# Revit family: Deca_Tubo de Ligação com Anel Expansor _1968.C.KID_Bacia Infantil
name_source: partatom
category: Plumbing Fixtures
revit_build: Autodesk Revit Architecture 2012 (Build: 20120126_0600(x64)
units: mm (PartAtom-declared; Revit-internal decimal feet)

## types (2) — shared parameters
Aprovado por = Contino/quattroD
Assembly Code = D2020300
Atendimento ao Cliente = 0800-0117073
Criado por = Contino/quattroD
Default Elevation = 250 mm  [stored 0.82021 ft]
Description = Tubo de ligação com anel expansor pra bacia infantil
Diâmetro Entrada Agua Fria = 40 mm  [stored 0.131234 ft]
Flow Pressure = 0.00 psi
Informações Complementares = Possui restritor de  vazão constante 8 L/min.
Linha = Tubo de ligação para bacia
Louça/Metais = Metal
Manufacturer = Deca
Material = Deca_Latão Cromado e Plástico de Engenharia
Model = Código
Norma = ABNT NBR 10283:2003
Peso Liquido (Kg) = 0.651
Produto = Tubo de ligação com anel expansor pra bacia infantil
Raio Entrada Agua Fria = 20 mm  [stored 0.0656168 ft]
Segmento = Competitivo
URL = www.deca.com.br/produtos
Variações de COR = Cromado (1968.C.KID); Branco (1968.E.KID.BR)
zero-valued in all types: CWFU, HWFU

## per-type parameters (varying)
| type | Código | Válvula |
| 1968.C.KID_Cromado CR10 | 1968.C.KID | Deca CR10 Cromado Metal |
| 1968.E.KID.BR_Branco BR16 | 1968.E.KID.BR | Deca BR16  Branco Metal |

note: [stored X ft] marks values corroborated as IEEE doubles in the binary element streams (Revit-internal decimal feet)

## geometry (parser evidence)
native form markers: Blend x2, Sweep x1
no freeform markers — native parametric forms only
